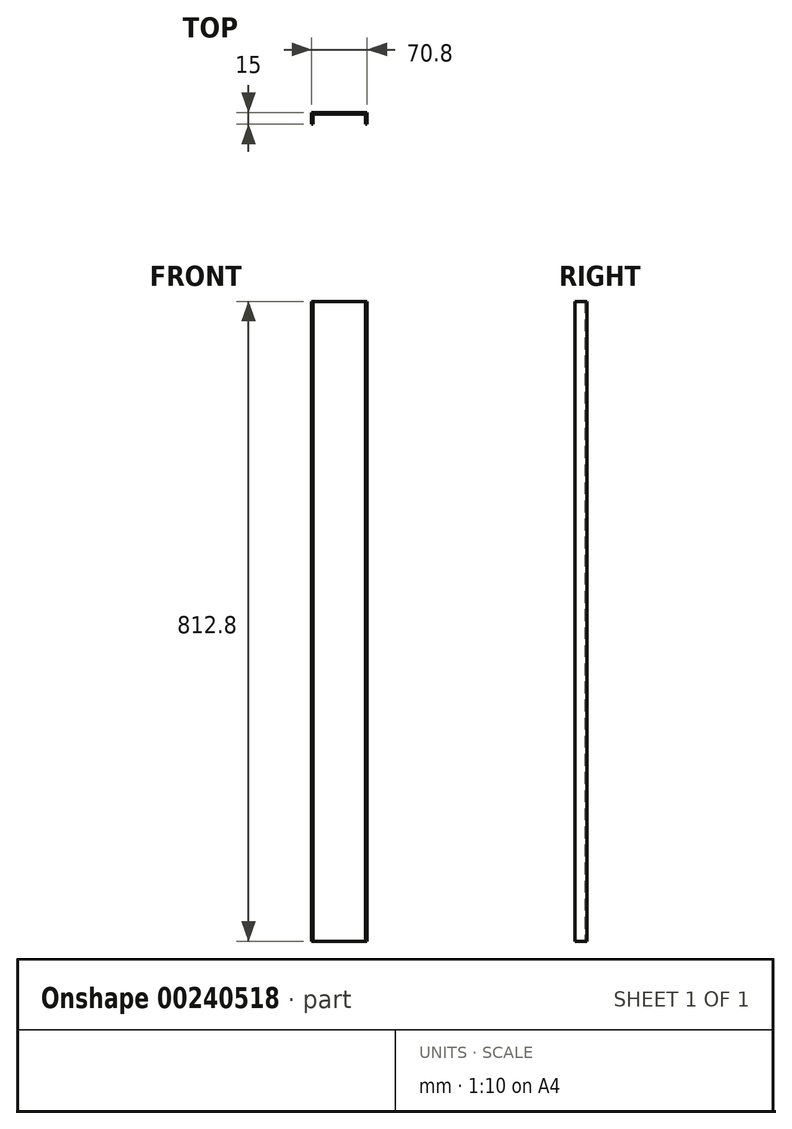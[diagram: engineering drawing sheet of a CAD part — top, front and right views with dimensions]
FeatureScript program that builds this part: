
annotation { "Feature Type Name" : "Feature", "Feature Type Description" : "" }
export const myFeature = defineFeature(function(context is Context, id is Id, definition is map)
    precondition{}
    {
        {
            var Q0;
            Q0=qCreatedBy(makeId("Top.planeOp"),FACE);
            var sketch = newSketch(context, id + "F0", { "sketchPlane" : qUnion([Q0])});
            skLineSegment(sketch, "E0", {"start": v(-52.47, 0) * mm, "end": v(-52.47, 15) * mm});
            skLineSegment(sketch, "E1", {"start": v(-52.47, 15) * mm, "end": v(18.33, 15) * mm});
            skLineSegment(sketch, "E2", {"start": v(18.33, 15) * mm, "end": v(18.33, 0) * mm});
            skLineSegment(sketch, "E3", {"start": v(18.33, 0) * mm, "end": v(16.33, 0) * mm});
            skLineSegment(sketch, "E4", {"start": v(16.33, 0) * mm, "end": v(16.33, 13) * mm});
            skLineSegment(sketch, "E5", {"start": v(16.33, 13) * mm, "end": v(-50.47, 13) * mm});
            skLineSegment(sketch, "E6", {"start": v(-50.47, 13) * mm, "end": v(-50.47, 0) * mm});
            skLineSegment(sketch, "E7", {"start": v(-50.47, 0) * mm, "end": v(-52.47, 0) * mm});
            skSolve(sketch);
        }
        {
            var Q0;
            Q0 = qSketchRegion(id + "F0", true);
            extrude(context, id + "F1", {"entities" : qUnion([Q0]), "depth" : 812.8 * mm});
        }
    });
